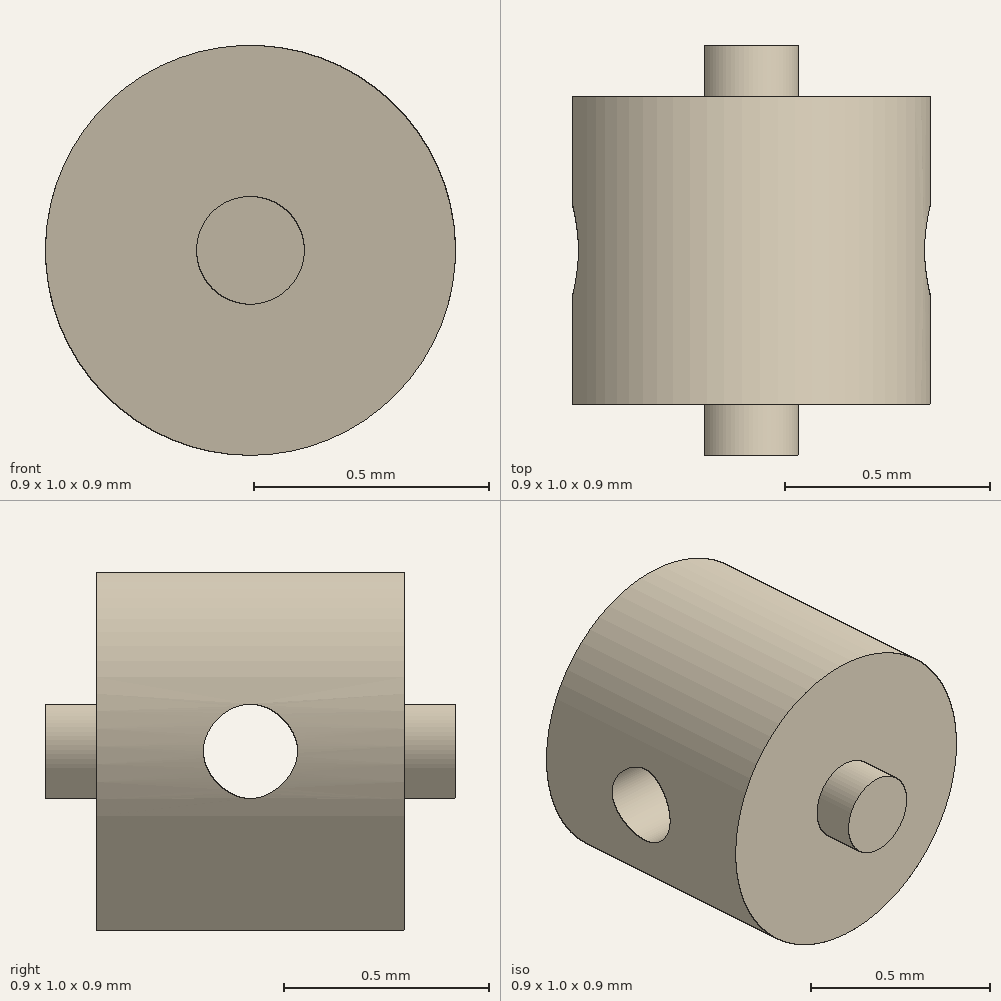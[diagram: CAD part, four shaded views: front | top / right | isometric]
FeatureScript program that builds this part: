
annotation { "Feature Type Name" : "Feature", "Feature Type Description" : "" }
export const myFeature = defineFeature(function(context is Context, id is Id, definition is map)
    precondition{}
    {
        {
            var Q0;
            Q0=qCreatedBy(makeId("Front.planeOp"),FACE);
            var sketch = newSketch(context, id + "F0", { "sketchPlane" : qUnion([Q0])});
            skCircle(sketch, "E0", {"center": v(0, 0) * mm, "radius": 0.12 * mm});
            skCircle(sketch, "E1", {"center": v(0, 0) * mm, "radius": 0.44 * mm});
            skSolve(sketch);
        }
        {
            var Q0;
            Q0=makeQuery(id+"F0.imprint","IMPRINT",FACE,{"disambiguationData":[TD([[makeQuery(id+"F0.imprint","IMPRINT",EDGE,{"derivedFrom":sQuery(id+"F0.wireOp",EDGE,"E0")}),-1.0]])]});
            extrude(context, id + "F1", {"entities" : qUnion([Q0]), "depth" : 0.75 * mm, "offsetDistance" : 25 * mm});
        }
        {
            var Q0;
            Q0=makeQuery(id+"F0.imprint","IMPRINT",FACE,{"disambiguationData":[TD([[makeQuery(id+"F0.imprint","IMPRINT",EDGE,{"derivedFrom":sQuery(id+"F0.wireOp",EDGE,"E0")}),1.0]])]});
            extrude(context, id + "F2", {"entities" : qUnion([Q0]), "operationType" : NewBodyOperationType.ADD, "depth" : 0.88 * mm, "offsetDistance" : 25 * mm, "hasSecondDirection" : true, "secondDirectionOppositeDirection" : true, "secondDirectionDepth" : 0.12 * mm});
        }
        {
            var Q0;
            Q0=qCreatedBy(makeId("Right.planeOp"),FACE);
            var sketch = newSketch(context, id + "F3", { "sketchPlane" : qUnion([Q0])});
            skCircle(sketch, "E2", {"center": v(-0.38, 0) * mm, "radius": 0.12 * mm});
            skSolve(sketch);
        }
        {
            var Q0;
            Q0 = qSketchRegion(id + "F3", true);
            extrude(context, id + "F4", {"entities" : qUnion([Q0]), "operationType" : NewBodyOperationType.REMOVE, "depth" : 25 * mm, "offsetDistance" : 25 * mm, "hasSecondDirection" : true, "secondDirectionOppositeDirection" : true, "secondDirectionDepth" : 25 * mm});
        }
    });
